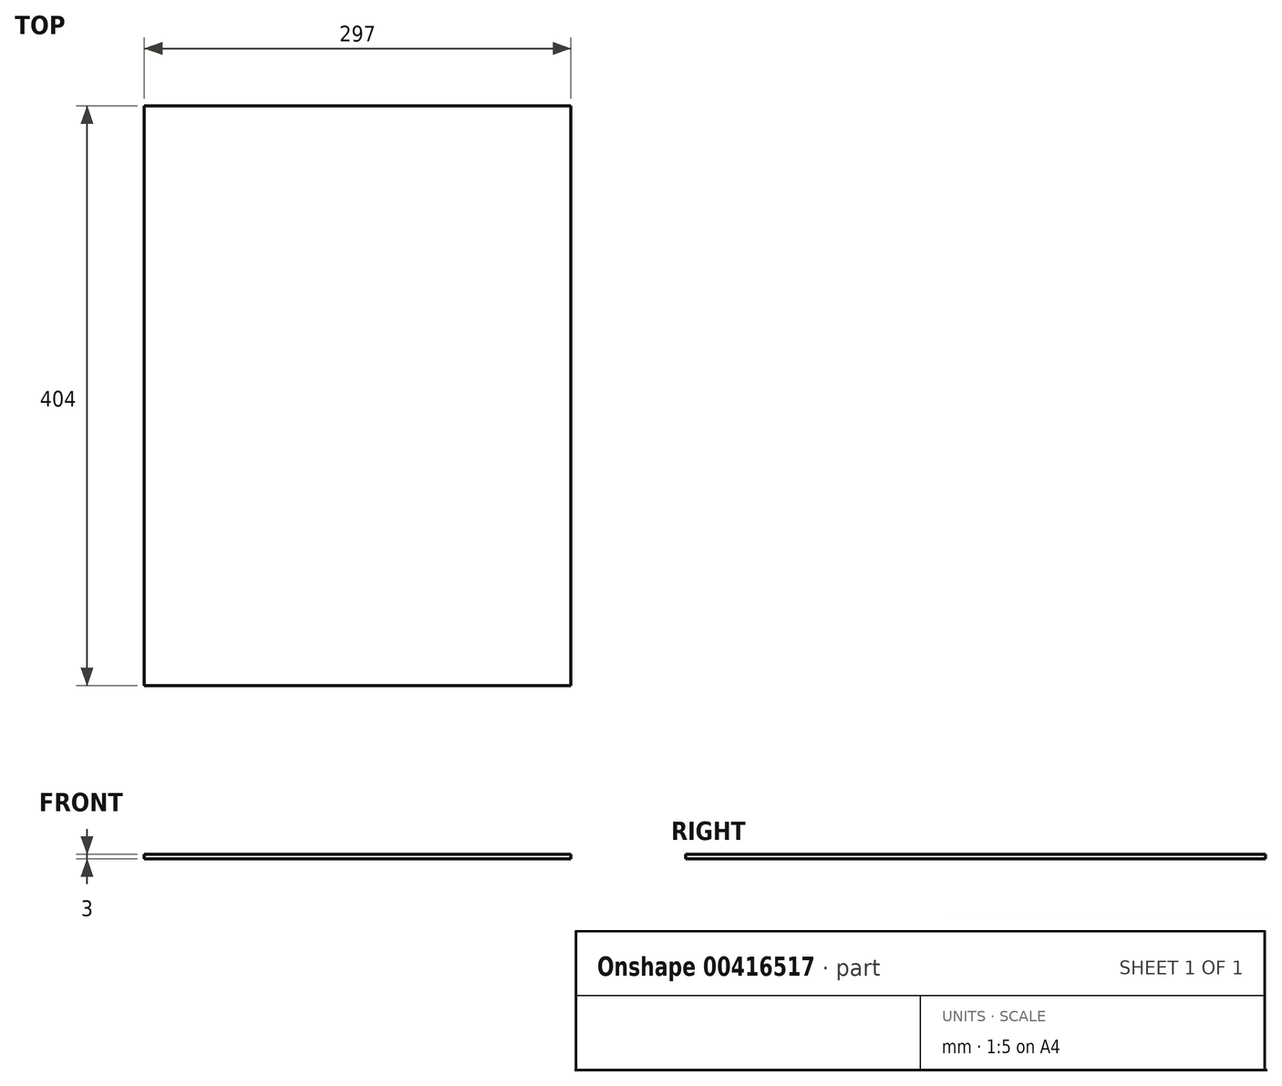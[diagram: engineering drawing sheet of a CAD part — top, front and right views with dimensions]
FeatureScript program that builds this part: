
annotation { "Feature Type Name" : "Feature", "Feature Type Description" : "" }
export const myFeature = defineFeature(function(context is Context, id is Id, definition is map)
    precondition{}
    {
        {
            var Q0;
            Q0=qCreatedBy(makeId("Top.planeOp"),FACE);
            var sketch = newSketch(context, id + "F0", { "sketchPlane" : qUnion([Q0])});
            skLineSegment(sketch, "E0.bottom", {"start": v(-148.5, 202) * mm, "end": v(148.5, 202) * mm});
            skLineSegment(sketch, "E0.top", {"start": v(-148.5, -202) * mm, "end": v(148.5, -202) * mm});
            skLineSegment(sketch, "E0.left", {"start": v(-148.5, 202) * mm, "end": v(-148.5, -202) * mm});
            skLineSegment(sketch, "E0.right", {"start": v(148.5, 202) * mm, "end": v(148.5, -202) * mm});
            skPoint(sketch, "E0.middle", {"position": v(0, 0) * mm});
            skSolve(sketch);
        }
        {
            var Q0;
            Q0 = qSketchRegion(id + "F0", true);
            extrude(context, id + "F1", {"entities" : qUnion([Q0]), "endBound" : BoundingType.SYMMETRIC, "depth" : 3 * mm});
        }
    });
